# Revit family: Faucet-Wall_Mount-Lavatory-KOHLER-Hone-K-22540IN
name_source: partatom
category: Plumbing Fixtures
units: mm (PartAtom-declared; Revit-internal decimal feet)

## family parameters
Cut with Voids When Loaded = No
Host = Face
OmniClass Number = 23.31.11.00
OmniClass Title = Faucets
Part Type = Normal
Room Calculation Point = No
Round Connector Dimension = Use Diameter
Shared = No

## types (3) — shared parameters
ADA Compliant = No
Assembly Code = D2010
CW Connection = Yes
Cold Water Inlet = Cold Water Inlet
Date Modified = 07/14/2024
Default Elevation = 36"
Description = SC Wall mount Lavatory faucet
Drain Included = No
Flow Rate = 2 GPM
HW Connection = Yes
Handle Clearance = 3 3/16"
Height = 3 1/4"
Hot Water Inlet = Hot Water Inlet
Length = 6 1/2"
Manufacturer = Kohler Co.
Master Format 2014 = 22 41 39
Master Format 2014 Name = Residential Faucets, Supplies, and Trim
Material = Premium Metal Construction
Pressure = 43.51 psi
Product Name = Hone
Spout Reach = 6 1/2"
URL = https://www.kohler.co.in
Vent Connection = No
Waste Connection = No
Waste Water Outlet = Waste Water Outlet
WaterSense Certified = No
Width = 7 11/16"

## per-type parameters (varying)
| type | Finish | Model | Product Page URL | Secondary Material | Type |
| CP-Polished Chrome | Kohler-Metal-CP-Polished_Chrome | K-22540IN-4ND-CP | https://www.kohler.co.in | Silicone-Pantone-423C | 1 |
| AF-Vibrant French Gold | Kohler-Metal-AF-Vibrant_French_Gold | K-22540IN-4ND-AF |  | Kohler-Metal-AF-Vibrant_French_Gold | 2 |
| BN-Vibrant Brushed Nickel | Kohler-Metal-BN-Vibrant_Brushed_Nickel | K-22540IN-4ND-BN |  | Silicone-Pantone-423C | 3 |

## geometry (parser evidence)
native form markers: Sweep x5
no freeform markers — native parametric forms only
